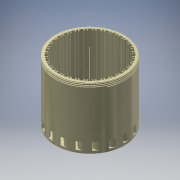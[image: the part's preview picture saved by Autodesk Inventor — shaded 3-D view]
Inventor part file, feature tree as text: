
AUTODESK INVENTOR PART (.ipt)
format: ipt  version: 2017 (Build 210142000, 142)  size: 974,848 bytes
history: native  units: mm
features: sketch x10, extrude x8, pattern_circular x4, fillet x1, sweep x1, chamfer x1, other x1
ambient origin geometry x8: Origin, YZ Plane, XZ Plane, XY Plane, X Axis, Y Axis, Z Axis, Center Point
bodies: Solid1 (feature_tree)
feature tree (26):
  extrude  "Extrusion1"  Depth=174.5mm
  extrude  "Extrusion2"  Depth=12.75mm
  pattern_circular  "Circular Pattern1"  Count=32 Angle=360.0deg
  extrude  "Extrusion3"  Depth=16.0mm
  pattern_circular  "Circular Pattern2"  [2 undecoded]
  extrude  "Extrusion4"  Depth=16.0mm
  extrude  "Extrusion5"  Depth=16.0mm
  pattern_circular  "Circular Pattern4"  [2 undecoded]
  extrude  "Extrusion6"  Depth=16.0mm TaperAngle=360.0deg
  fillet  "Fillet2"  Radius=35.0mm
  pattern_circular  "Circular Pattern5"  [2 undecoded]
  sweep  "Sweep2"
  extrude  "Extrusion11"  Depth=25.0mm
  chamfer  "Chamfer3"  Distance=30.0mm
  extrude  "Extrusion12"  Depth=16.0mm TaperAngle=360.0deg
  sketch  "Sketch1"  dims[d0=280.0mm d17=174.5mm]
  sketch  "Sketch2"  dims[d40=203.2mm d41=0.0mm d42=12.75mm]
  sketch  "Sketch4"  dims[d43=6.4mm]
  sketch  "Sketch5"  dims[d44=2.0mm]
  sketch  "Sketch6"  dims[d45=1.0mm]
  sketch  "Sketch7"  dims[d46=244.0mm]
  sketch  "Sketch15"  dims[d47=123.0mm]
  sketch  "3D Sketch2"
  other  "Helical Curve3"
  sketch  "Sketch16"  dims[d48=152.4mm d49=0.0mm d50=320.0mm d51=360.0deg]
  sketch  "Sketch17"  dims[d54=6.4mm d55=6.4mm d56=6.4mm d57=1.0mm d58=1.0mm d59=152.4mm d60=0.0mm d61=320.0mm d62=360.0deg d69=35.0mm d70=0.0mm d71=10.0mm d72=120.0deg d74=25.0mm d75=30.0mm d76=0.0mm d77=180.0mm d78=360.0deg d80=10.0mm d81=0.0mm d82=16.0mm d90=20.0mm d91=180.0mm d92=360.0deg d139=1.0mm d141=120.0deg d142=3.0mm d143=6.0mm d144=45.0mm d145=241.87mm d146=0.0mm d147=0.0mm d148=0.0mm d149=18.0mm d150=18.0mm d151=40.0mm d152=20.0mm d153=0.0mm d154=20.0mm d155=2.0mm d156=13.823008mm d157=50.0mm d158=16.0mm d159=0.0mm]
note: 6 required parameter values undecoded (feature->parameter linkage not recoverable at this tier; creation-order binding heuristic only, values carry confidence <= 0.55)
